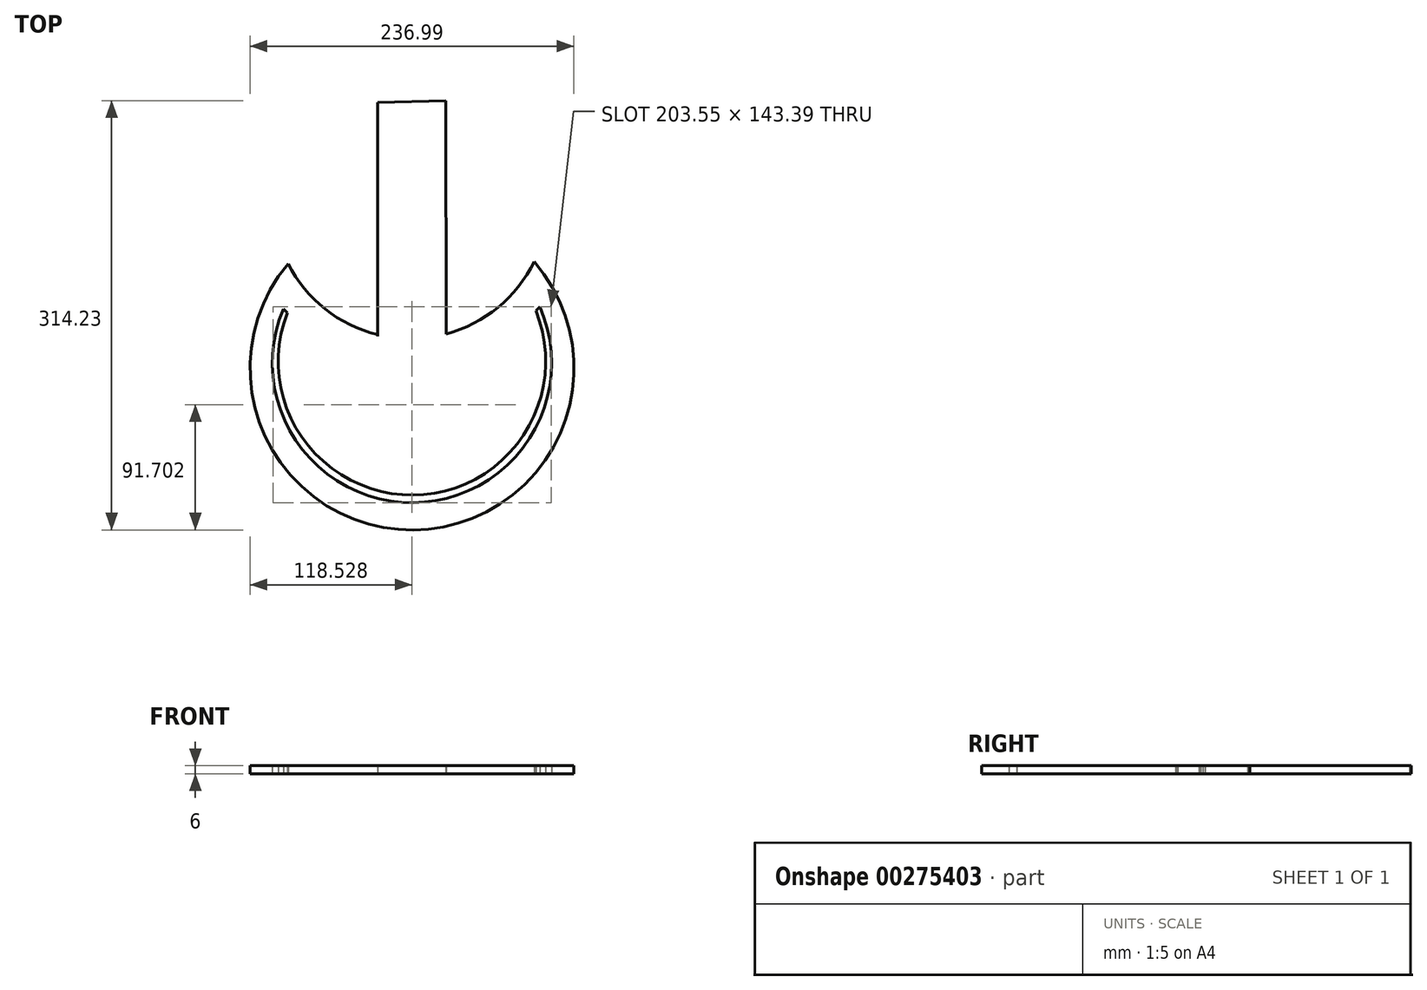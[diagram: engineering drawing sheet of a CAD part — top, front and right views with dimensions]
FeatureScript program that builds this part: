
annotation { "Feature Type Name" : "Feature", "Feature Type Description" : "" }
export const myFeature = defineFeature(function(context is Context, id is Id, definition is map)
    precondition{}
    {
        {
            var Q0;
            Q0=qCreatedBy(makeId("Top.planeOp"),FACE);
            var sketch = newSketch(context, id + "F0", { "sketchPlane" : qUnion([Q0])});
            skPoint(sketch, "E0.start.orphan", {"position": v(-125, -132.75) * mm});
            skLineSegment(sketch, "E1", {"start": v(0, 0) * mm, "end": v(4.89, -189.33) * mm, "construction": true});
            skPoint(sketch, "E1.endSnap0", {"position": v(4.89, -64.78) * mm});
            skLineSegment(sketch, "E2", {"start": v(4.89, -189.33) * mm, "end": v(5.87, -312.36) * mm});
            skPoint(sketch, "E2.endSnap0", {"position": v(5.87, -212.77) * mm});
            skArc(sketch, "E3", {"start": v(-85.55, -134.55) * mm, "mid": v(6.15, -329.32) * mm, "end": v(94.46, -133) * mm});
            skArc(sketch, "E4", {"start": v(-85.55, -134.55) * mm, "mid": v(4.94, -189.33) * mm, "end": v(94.46, -133) * mm});
            skPoint(sketch, "E5.startSnap0", {"position": v(4.94, -189.33) * mm});
            skLineSegment(sketch, "E6.bottom", {"start": v(-20.06, -187.4) * mm, "end": v(-20.06, -187.4) * mm});
            skLineSegment(sketch, "E7.bottom", {"start": v(29.94, -187.4) * mm, "end": v(29.94, -187.4) * mm});
            skLineSegment(sketch, "E8", {"start": v(30.06, -185.92) * mm, "end": v(29.94, -187.4) * mm});
            skLineSegment(sketch, "E9", {"start": v(-20.16, -186.37) * mm, "end": v(-20.06, -187.4) * mm});
            skArc(sketch, "E10", {"start": v(-77.73, -147.35) * mm, "mid": v(5.97, -309.32) * mm, "end": v(86.87, -145.93) * mm});
            skArc(sketch, "E11", {"start": v(-75.5, -150.35) * mm, "mid": v(5.98, -303.75) * mm, "end": v(84.71, -148.93) * mm});
            skLineSegment(sketch, "E12", {"start": v(-89, -167.35) * mm, "end": v(-86.1, -170.35) * mm});
            skLineSegment(sketch, "E13", {"start": v(95.74, -168.93) * mm, "end": v(98.56, -165.93) * mm});
            skLineSegment(sketch, "E14", {"start": v(-20.06, -16.4) * mm, "end": v(29.94, -15.1) * mm});
            skLineSegment(sketch, "E15", {"start": v(-20.06, -16.4) * mm, "end": v(-20.06, -187.4) * mm});
            skLineSegment(sketch, "E16", {"start": v(29.94, -15.1) * mm, "end": v(30.06, -185.92) * mm});
            skSolve(sketch);
        }
        {
            var Q0;
            Q0=makeQuery(id+"F0.imprint","IMPRINT",FACE,{"disambiguationData":[TD([[makeQuery(id+"F0.imprint","IMPRINT",EDGE,{"derivedFrom":sQuery(id+"F0.wireOp",EDGE,"03166fc7-ecd7-4f26-9a16-ad492ba4d284.bottom")}),-1.0]])]});
            var Q1;
            {var subQ0=sQuery(id+"F0.wireOp",EDGE,"E4");var subQ1=sQuery(id+"F0.wireOp",EDGE,"E2");var subQ2=makeQuery(id+"F0.imprint","INTERSECT",VERTEX,{"derivedFrom":[subQ1,subQ0]});Q1=makeQuery(id+"F0.imprint","IMPRINT",FACE,{"disambiguationData":[TD([[makeQuery(id+"F0.imprint","IMPRINT",EDGE,{"disambiguationData":[TD([[subQ2,-1.0]])],"derivedFrom":subQ1}),1.0]])]});}
            var Q2;
            {var subQ4=sQuery(id+"F0.wireOp",EDGE,"E3");Q2=makeQuery(id+"F0.imprint","IMPRINT",FACE,{"disambiguationData":[TD([[makeQuery(id+"F0.imprint","IMPRINT",EDGE,{"derivedFrom":subQ4}),1.0]])]});}
            var Q3;
            {var subQ0=sQuery(id+"F0.wireOp",EDGE,"E4");var subQ1=sQuery(id+"F0.wireOp",EDGE,"E2");var subQ2=makeQuery(id+"F0.imprint","INTERSECT",VERTEX,{"derivedFrom":[subQ1,subQ0]});Q3=makeQuery(id+"F0.imprint","IMPRINT",FACE,{"disambiguationData":[TD([[makeQuery(id+"F0.imprint","IMPRINT",EDGE,{"disambiguationData":[TD([[subQ2,-1.0]])],"derivedFrom":subQ1}),-1.0]])]});}
            var Q4;
            {var subQ5=sQuery(id+"F0.wireOp",EDGE,"E12");Q4=makeQuery(id+"F0.imprint","IMPRINT",FACE,{"disambiguationData":[TD([[makeQuery(id+"F0.imprint","IMPRINT",EDGE,{"derivedFrom":subQ5}),1.0]])]});}
            var Q5;
            {var subQ5=sQuery(id+"F0.wireOp",EDGE,"E13");Q5=makeQuery(id+"F0.imprint","IMPRINT",FACE,{"disambiguationData":[TD([[makeQuery(id+"F0.imprint","IMPRINT",EDGE,{"derivedFrom":subQ5}),1.0]])]});}
            var Q6;
            {var subQ1=sQuery(id+"F0.wireOp",EDGE,"E14");Q6=makeQuery(id+"F0.imprint","IMPRINT",FACE,{"disambiguationData":[TD([[makeQuery(id+"F0.imprint","IMPRINT",EDGE,{"derivedFrom":subQ1}),-1.0]])]});}
            extrude(context, id + "F1", {"entities" : qUnion([Q0, Q1, Q2, Q3, Q4, Q5, Q6]), "depth" : 6 * mm, "offsetDistance" : 25 * mm});
        }
    });
